# Revit family: AAC51
name_source: partatom
category: Furniture
revit_build: Autodesk Revit 2016 (Build: 20161004_0715(x64)
units: mm (PartAtom-declared; Revit-internal decimal feet)

## family parameters
Always vertical = Yes
Cut with Voids When Loaded = No
OmniClass Number = 23.40.20.00
OmniClass Title = General Furniture and Specialties
Room Calculation Point = No
Shared = No
Work Plane-Based = No

## types (1)
- AAC51
    Base = HAY Black powder coated aluminum - Soft Black
    Base gaslift = HAY Chrome
    Depth = 69cm - 27.17inch
    Description = Height-adjustable swivel office chair with upholstered shell and aluminium frame with five-star castor base. Suitable for executive or official settings and work-at-home offices.
    Design = Hee Welling & HAY
    Height = 87.50m - 34.45inch
    Manufacturer = HAY
    Model = AAC 51 Wheel base
    Optional Upholstery = Full upholstery quilted, Full upholstery
    Price = Contact HAY or visit hay.dk
    Seat Height = 42.40cm - 16.69inch
    Shell = HAY Hallingdal - 130
    Strength, durability and safety = EN 16139:2013 L2
    Type Comments = Injection moulded polypropylene shell with full upholstery and choice of plain or quilted seat.
    URL = http://hay.dk
    Upholstery fabric = Available in a large selection of standard fabrics and leathers.
    Variations = Available in a large selection of shell colours and base finishes. Other base options are:  4-leg steel base, swivel base, sled base, solid wood legs and moulded plywood legs. Shell is also available without armrest.
    Wheels = HAY Black Plastic
    Width = 69cm - 27.17inch

## geometry (parser evidence)
native form markers: Sweep x2
no freeform markers — native parametric forms only
